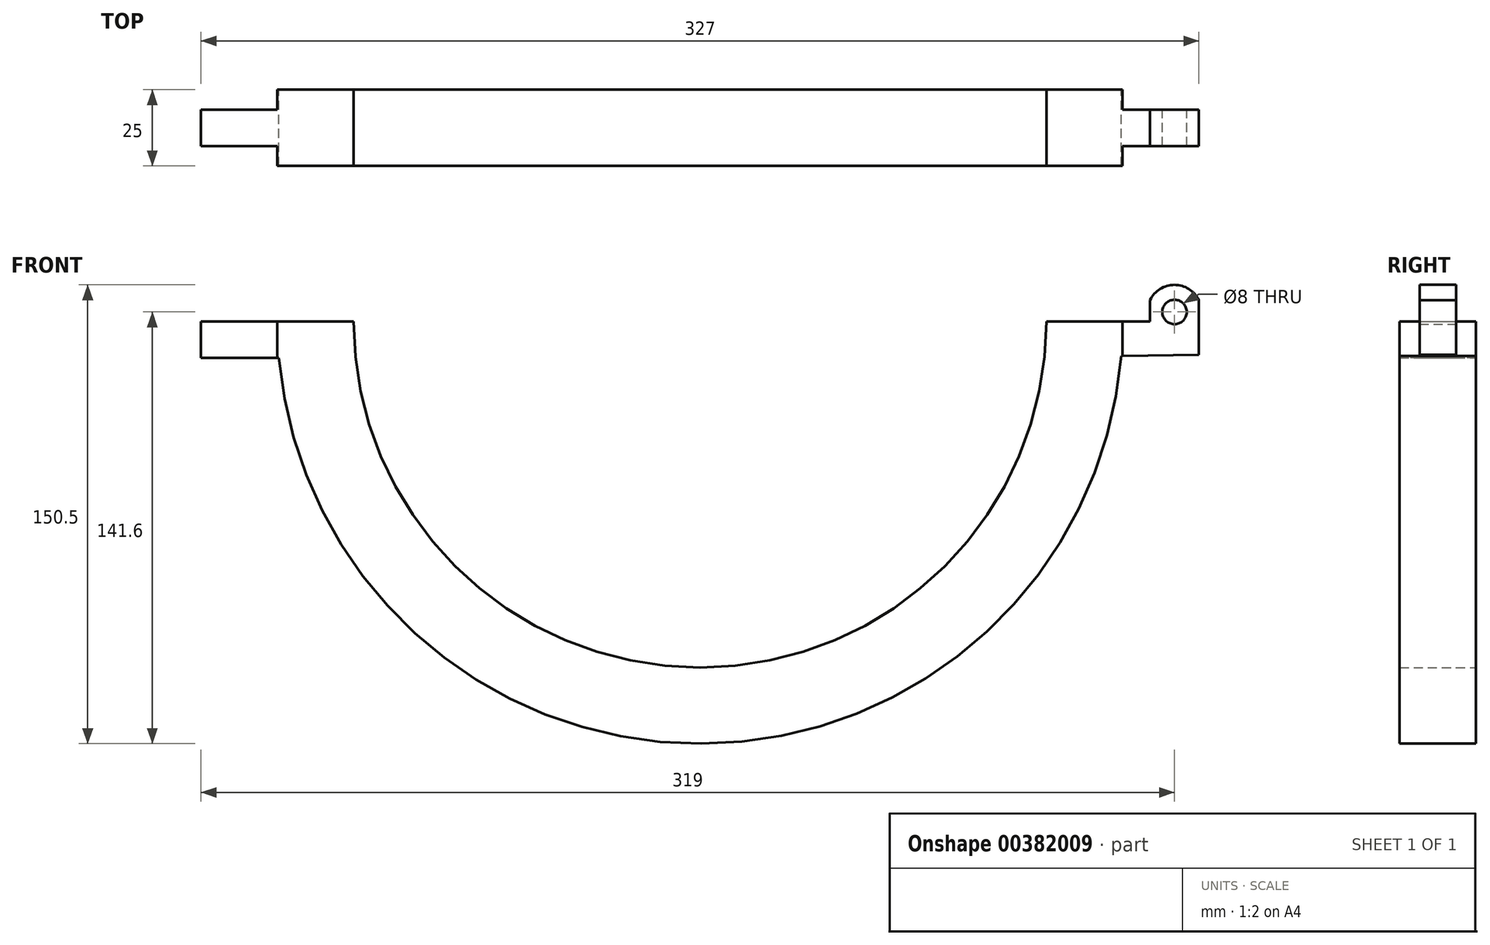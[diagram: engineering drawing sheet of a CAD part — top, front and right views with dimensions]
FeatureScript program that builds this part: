
annotation { "Feature Type Name" : "Feature", "Feature Type Description" : "" }
export const myFeature = defineFeature(function(context is Context, id is Id, definition is map)
    precondition{}
    {
        {
            var Q0;
            Q0=qCreatedBy(makeId("Front.planeOp"),FACE);
            var sketch = newSketch(context, id + "F0", { "sketchPlane" : qUnion([Q0])});
            skArc(sketch, "E0", {"start": v(-113.5, 0) * mm, "mid": v(0, -113.5) * mm, "end": v(113.5, 0) * mm});
            skLineSegment(sketch, "E1", {"start": v(-138.5, 0) * mm, "end": v(-113.5, 0) * mm});
            skArc(sketch, "E2.0", {"start": v(-137.98, -12) * mm, "mid": v(0.33, -138.5) * mm, "end": v(138.03, -11.34) * mm});
            skLineSegment(sketch, "E3.bottom", {"start": v(163.5, -11) * mm, "end": v(138.03, -11.34) * mm});
            skLineSegment(sketch, "E4", {"start": v(163.5, -11) * mm, "end": v(163.5, 7) * mm});
            skArc(sketch, "E5", {"start": v(163.5, 7) * mm, "mid": v(155.5, 12) * mm, "end": v(147.5, 7) * mm});
            skPoint(sketch, "E6.end.orphan", {"position": v(147.5, -11) * mm});
            skLineSegment(sketch, "E7", {"start": v(147.5, 7) * mm, "end": v(147.5, 0) * mm});
            skLineSegment(sketch, "E8", {"start": v(147.5, 0) * mm, "end": v(138.5, 0) * mm});
            skLineSegment(sketch, "E9.trimOffspring", {"start": v(113.5, 0) * mm, "end": v(138.5, 0) * mm});
            skLineSegment(sketch, "E10.right", {"start": v(163.5, 0) * mm, "end": v(163.5, 7) * mm});
            skPoint(sketch, "E10.middle", {"position": v(138.5, 0) * mm});
            skLineSegment(sketch, "E11", {"start": v(138.5, 0) * mm, "end": v(163.5, 0) * mm});
            skPoint(sketch, "E12.middle", {"position": v(-138.5, 0) * mm});
            skLineSegment(sketch, "E13", {"start": v(-138.5, 0) * mm, "end": v(-163.5, 0) * mm});
            skLineSegment(sketch, "E14.MirrorCS", {"start": v(-163.5, -12) * mm, "end": v(-137.98, -12) * mm});
            skLineSegment(sketch, "E15.MirrorCS", {"start": v(-163.5, 0) * mm, "end": v(-163.5, -12) * mm});
            skCircle(sketch, "E16", {"center": v(155.5, 3.1) * mm, "radius": 4 * mm});
            skSolve(sketch);
        }
        {
            var Q0;
            Q0=qSketchRegion(id+"F0",true);
            extrude(context, id + "F1", {"entities" : qUnion([Q0]), "endBound" : BoundingType.SYMMETRIC, "depth" : 25 * mm});
        }
        {
            var Q0;
            Q0=makeQuery(id+"F1.opExtrude","SWEPT_FACE",FACE,{"disambiguationData":[OSD([sQuery(id+"F0.wireOp",EDGE,"E4"),sQuery(id+"F0.wireOp",EDGE,"E10.right")])]});
            var sketch = newSketch(context, id + "F2", { "sketchPlane" : qUnion([Q0])});
            skLineSegment(sketch, "E17.bottom", {"start": v(-14.67, 18.2) * mm, "end": v(-6, 18.2) * mm});
            skLineSegment(sketch, "E17.top", {"start": v(-14.67, -19) * mm, "end": v(-6, -19) * mm});
            skLineSegment(sketch, "E17.left", {"start": v(-14.67, 18.2) * mm, "end": v(-14.67, -19) * mm});
            skLineSegment(sketch, "E17.right", {"start": v(-6, 18.2) * mm, "end": v(-6, -19) * mm});
            skLineSegment(sketch, "E18.bottom", {"start": v(6, 17.04) * mm, "end": v(17.77, 17.04) * mm});
            skLineSegment(sketch, "E18.top", {"start": v(6, -20.3) * mm, "end": v(17.77, -20.3) * mm});
            skLineSegment(sketch, "E18.left", {"start": v(6, 17.04) * mm, "end": v(6, -20.3) * mm});
            skLineSegment(sketch, "E18.right", {"start": v(17.77, 17.04) * mm, "end": v(17.77, -20.3) * mm});
            skSolve(sketch);
        }
        {
            var Q0;
            Q0=qSketchRegion(id+"F2",true);
            extrude(context, id + "F3", {"entities" : qUnion([Q0]), "operationType" : NewBodyOperationType.REMOVE, "oppositeDirection" : true, "depth" : 25 * mm});
        }
        {
            var Q0;
            Q0=makeQuery(id+"F1.opExtrude","SWEPT_FACE",FACE,{"disambiguationData":[OSD([sQuery(id+"F0.wireOp",EDGE,"E15.MirrorCS")])]});
            var sketch = newSketch(context, id + "F4", { "sketchPlane" : qUnion([Q0])});
            skLineSegment(sketch, "E19.bottom", {"start": v(-16.38, 7) * mm, "end": v(-6, 7) * mm});
            skLineSegment(sketch, "E19.top", {"start": v(-16.38, -19.08) * mm, "end": v(-6, -19.08) * mm});
            skLineSegment(sketch, "E19.left", {"start": v(-16.38, 7) * mm, "end": v(-16.38, -19.08) * mm});
            skLineSegment(sketch, "E19.right", {"start": v(-6, 7) * mm, "end": v(-6, -19.08) * mm});
            skLineSegment(sketch, "E20.bottom", {"start": v(6, 6.66) * mm, "end": v(18.87, 6.66) * mm});
            skLineSegment(sketch, "E20.top", {"start": v(6, -20.63) * mm, "end": v(18.87, -20.63) * mm});
            skLineSegment(sketch, "E20.left", {"start": v(6, 6.66) * mm, "end": v(6, -20.63) * mm});
            skLineSegment(sketch, "E20.right", {"start": v(18.87, 6.66) * mm, "end": v(18.87, -20.63) * mm});
            skSolve(sketch);
        }
        {
            var Q0;
            Q0=qSketchRegion(id+"F4",true);
            extrude(context, id + "F5", {"entities" : qUnion([Q0]), "operationType" : NewBodyOperationType.REMOVE, "oppositeDirection" : true, "depth" : 25 * mm});
        }
    });
